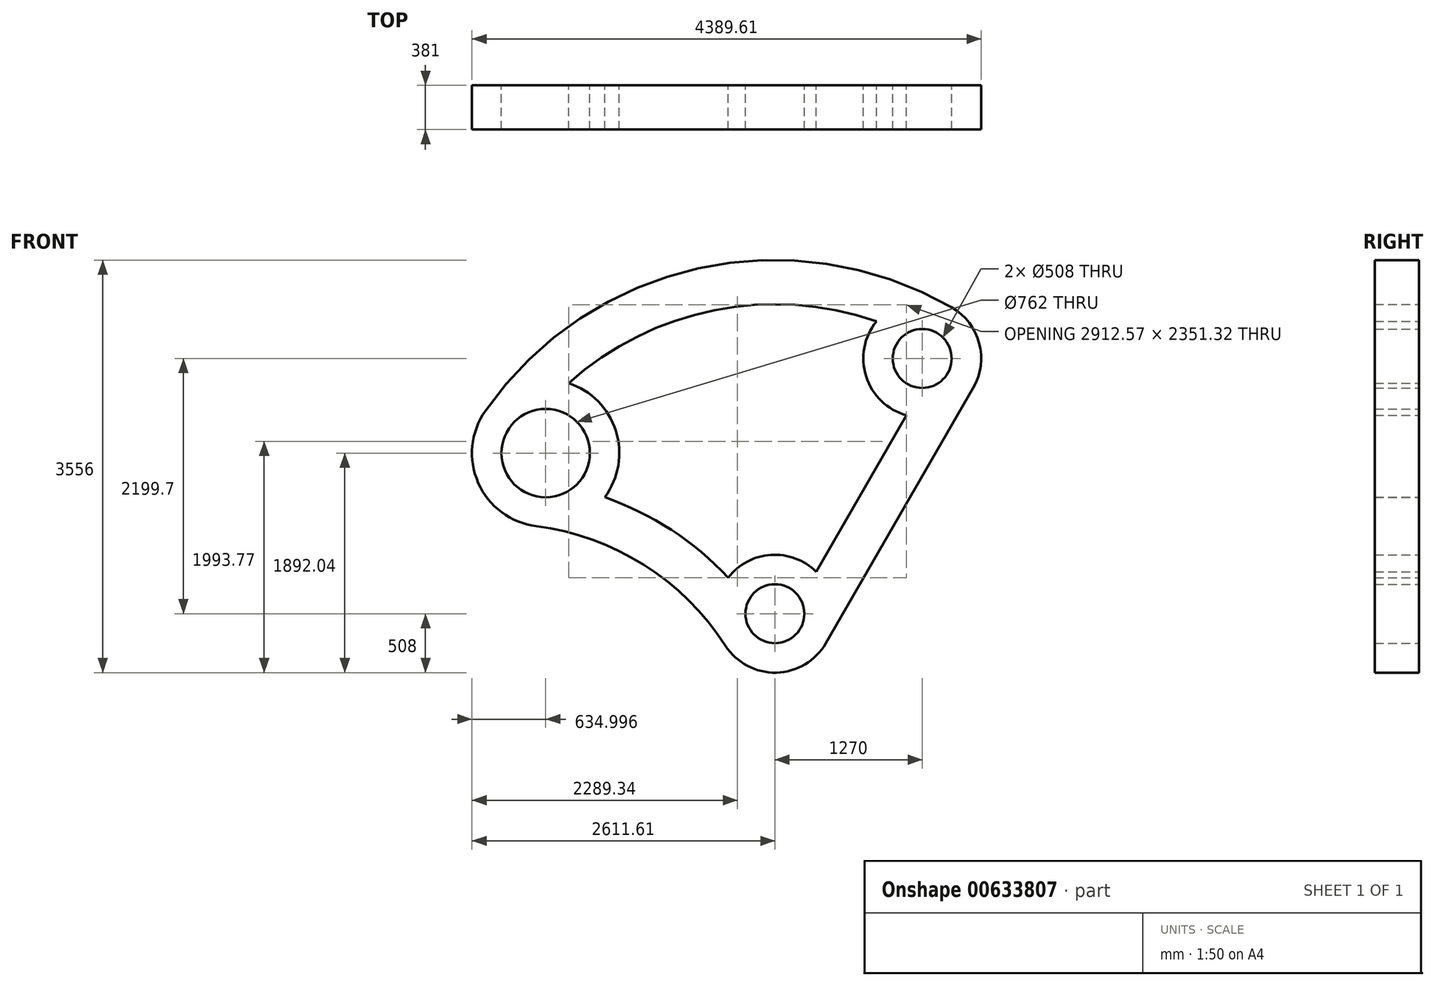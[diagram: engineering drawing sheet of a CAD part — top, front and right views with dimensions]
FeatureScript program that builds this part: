
annotation { "Feature Type Name" : "Feature", "Feature Type Description" : "" }
export const myFeature = defineFeature(function(context is Context, id is Id, definition is map)
    precondition{}
    {
        {
            var Q0;
            Q0=qCreatedBy(makeId("Front.planeOp"),FACE);
            var sketch = newSketch(context, id + "F0", { "sketchPlane" : qUnion([Q0])});
            skArc(sketch, "E0", {"start": v(1524, 2639.65) * mm, "mid": v(-659.7, 2975.75) * mm, "end": v(-2496.78, 1748.26) * mm});
            skArc(sketch, "E1", {"start": v(-1467.8, 1004.14) * mm, "mid": v(-1371.14, 1575.41) * mm, "end": v(-1778.56, 1987.36) * mm});
            skArc(sketch, "E2", {"start": v(1709.94, 1945.7) * mm, "mid": v(1760.7, 2331.18) * mm, "end": v(1524, 2639.65) * mm});
            skCircle(sketch, "E3", {"center": v(-1976.61, 1384.04) * mm, "radius": 381 * mm});
            skCircle(sketch, "E4", {"center": v(1270, 2199.7) * mm, "radius": 254 * mm});
            skArc(sketch, "E5", {"start": v(355.95, 362.44) * mm, "mid": v(-34.97, 506.8) * mm, "end": v(-402.36, 310.11) * mm});
            skCircle(sketch, "E6", {"center": v(0, 0) * mm, "radius": 254 * mm});
            skArc(sketch, "E7.trimOffspring", {"start": v(-427.05, -275.12) * mm, "mid": v(-1128.45, 419.87) * mm, "end": v(-2057.52, 754.22) * mm});
            skLineSegment(sketch, "E8", {"start": v(439.94, -254) * mm, "end": v(1709.94, 1945.7) * mm});
            skArc(sketch, "E9.trimOffspring", {"start": v(-402.36, 310.11) * mm, "mid": v(-893.11, 721.55) * mm, "end": v(-1467.8, 1004.14) * mm});
            skLineSegment(sketch, "E10.trimOffspring", {"start": v(355.95, 362.44) * mm, "end": v(1134.01, 1710.24) * mm});
            skArc(sketch, "E11.trimOffspring", {"start": v(-427.05, -275.12) * mm, "mid": v(12.37, -507.85) * mm, "end": v(439.94, -254) * mm});
            skArc(sketch, "E12.trimOffspring", {"start": v(875.17, 2519.36) * mm, "mid": v(-524.2, 2615) * mm, "end": v(-1778.56, 1987.36) * mm});
            skArc(sketch, "E13.trimOffspring", {"start": v(-2496.78, 1748.26) * mm, "mid": v(-2557.43, 1127.38) * mm, "end": v(-2057.52, 754.22) * mm});
            skArc(sketch, "E14.trimOffspring", {"start": v(875.17, 2519.36) * mm, "mid": v(786.16, 2044.92) * mm, "end": v(1134.01, 1710.24) * mm});
            skSolve(sketch);
        }
        {
            var Q0;
            Q0=makeQuery(id+"F0.imprint","IMPRINT",FACE,{"disambiguationData":[TD([[makeQuery(id+"F0.imprint","IMPRINT",EDGE,{"derivedFrom":sQuery(id+"F0.wireOp",EDGE,"E0")}),1.0]])]});
            extrude(context, id + "F1", {"entities" : qUnion([Q0]), "depth" : 381 * mm, "offsetDistance" : 25.4 * mm});
        }
    });
